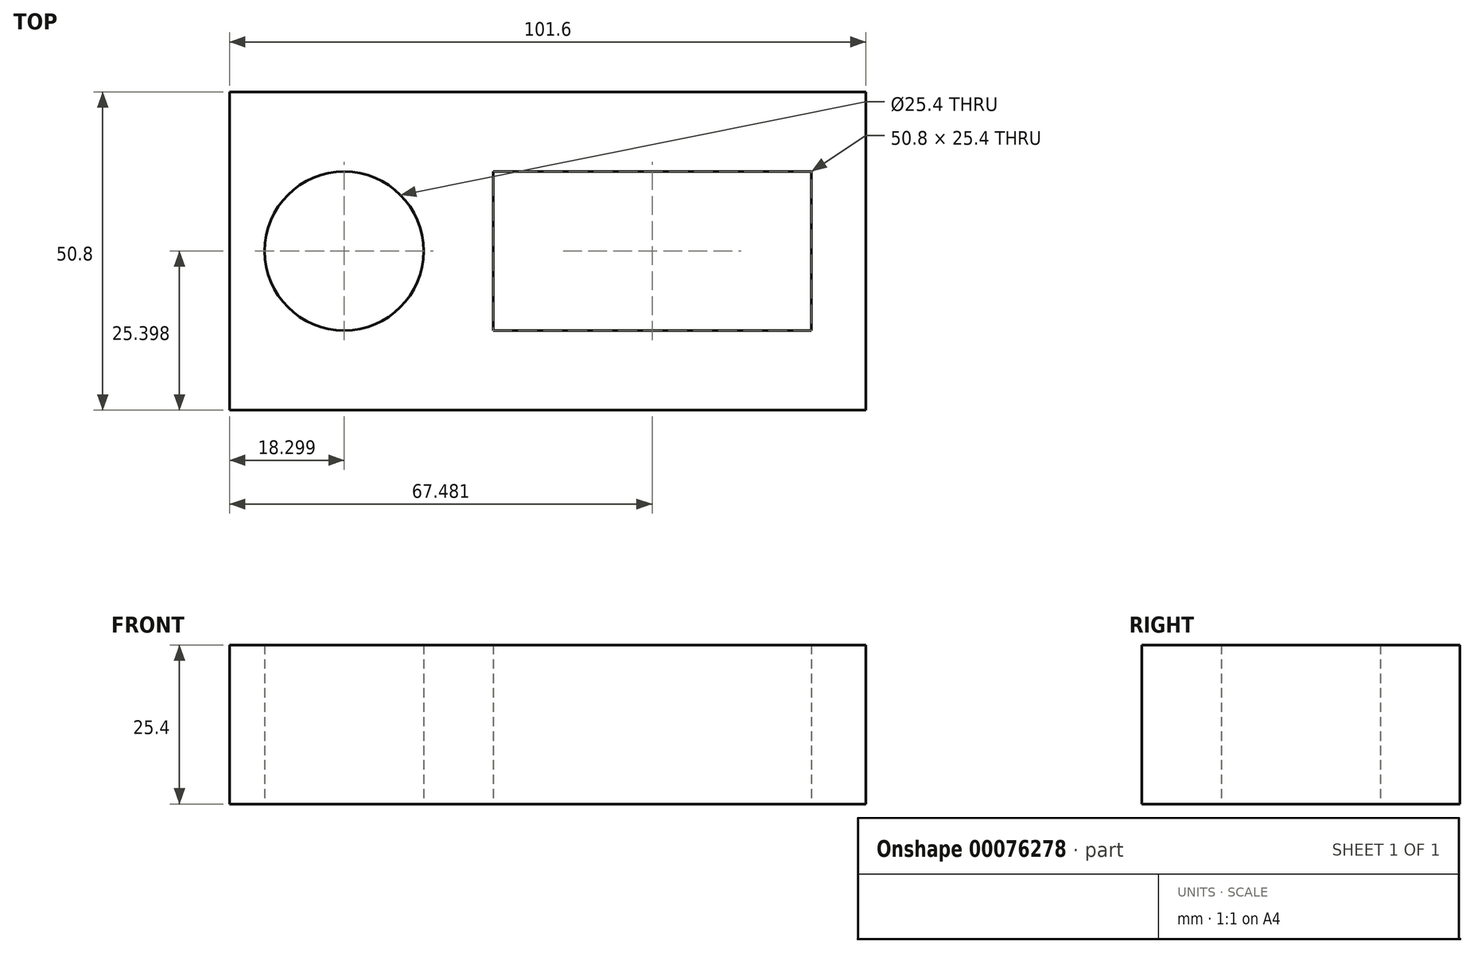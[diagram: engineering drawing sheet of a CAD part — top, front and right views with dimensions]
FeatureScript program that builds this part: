
annotation { "Feature Type Name" : "Feature", "Feature Type Description" : "" }
export const myFeature = defineFeature(function(context is Context, id is Id, definition is map)
    precondition{}
    {
        {
            var Q0;
            Q0=qCreatedBy(makeId("Top.planeOp"),FACE);
            var sketch = newSketch(context, id + "F0", { "sketchPlane" : qUnion([Q0])});
            skLineSegment(sketch, "E0.bottom", {"start": v(-118.44, 74.8) * mm, "end": v(-16.84, 74.8) * mm});
            skLineSegment(sketch, "E0.top", {"start": v(-118.44, 24) * mm, "end": v(-16.84, 24) * mm});
            skLineSegment(sketch, "E0.left", {"start": v(-118.44, 74.8) * mm, "end": v(-118.44, 24) * mm});
            skLineSegment(sketch, "E0.right", {"start": v(-16.84, 74.8) * mm, "end": v(-16.84, 24) * mm});
            skCircle(sketch, "E1", {"center": v(-100.14, 49.4) * mm, "radius": 12.7 * mm});
            skPoint(sketch, "E1.centerSnap0", {"position": v(-118.44, 49.4) * mm});
            skLineSegment(sketch, "E2.bottom", {"start": v(-25.56, 62.1) * mm, "end": v(-76.36, 62.1) * mm});
            skLineSegment(sketch, "E2.top", {"start": v(-25.56, 36.7) * mm, "end": v(-76.36, 36.7) * mm});
            skLineSegment(sketch, "E2.left", {"start": v(-25.56, 62.1) * mm, "end": v(-25.56, 36.7) * mm});
            skLineSegment(sketch, "E2.right", {"start": v(-76.36, 62.1) * mm, "end": v(-76.36, 36.7) * mm});
            skSolve(sketch);
        }
        {
            var Q0;
            Q0=makeQuery(id+"F0.imprint","IMPRINT",FACE,{"disambiguationData":[TD([[makeQuery(id+"F0.imprint","IMPRINT",EDGE,{"derivedFrom":sQuery(id+"F0.wireOp",EDGE,"E0.bottom")}),-1.0]])]});
            extrude(context, id + "F1", {"entities" : qUnion([Q0]), "depth" : 25.4 * mm});
        }
    });
